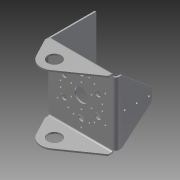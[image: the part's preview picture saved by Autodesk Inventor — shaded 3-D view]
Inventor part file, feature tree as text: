
AUTODESK INVENTOR PART (.ipt)
format: ipt  version: 2014 (Build 180170000, 170)  size: 277,504 bytes
history: native  units: in
note: dims shown in document units (in); Inventor stores cm internally (conversion verified against a paired STEP export)
features: sheet_metal_op x10, sketch x8, other x8, reference x4, fillet x2
ambient origin geometry x8: Origin, YZ Plane, XZ Plane, XY Plane, X Axis, Y Axis, Z Axis, Center Point
bodies: Solid1 (feature_tree)
feature tree (32):
  sheet_metal_op  "Face1"
  sheet_metal_op  "Flange2"
  fillet  "Fillet1"  Radius=0.125in
  sheet_metal_op  "Flange3"
  fillet  "Fillet2"  Radius=0.125in
  sheet_metal_op  "Flange4"
  sketch  "Sketch1"  dims[d1=2.3622in d2=5.25in d3=1.125in d4=0.503in d5=1.625in d6=1.31in d7=0.1875in d8=0.1875in d9=0.1875in d10=0.1875in d11=360.0deg d12=0.125in d23=0.125in]
  other  "Plate1"
  sketch  "Sketch3"  dims[d24=0.0625in]
  other  "Plate3"
  sheet_metal_op  "Bend2"
  sheet_metal_op  "Corner2"
  sketch  "Sketch5"  dims[d25=0.25in]
  reference  "Reference2"
  sketch  "Sketch6"  dims[d26=0.125in]
  sketch  "Sketch7"  dims[d27=3.0in d28=90.0deg d29=0.125in]
  other  "Plate4"
  sheet_metal_op  "Bend3"
  sheet_metal_op  "Corner3"
  sketch  "Sketch8"  dims[d30=0.5in]
  sketch  "Sketch9"  dims[d31=0.125in]
  reference  "Reference3"
  reference  "Reference4"
  reference  "Reference5"
  sketch  "Sketch11"  dims[d32=0.125in d39=1.125in d40=100.0in d41=0.0in d42=2.25in d43=0.25in d44=0.25in d45=10.0in d46=0.0in d47=0.125in d48=0.125in d49=0.0625in d50=0.25in d51=0.125in d52=3.0in d53=90.0deg d54=0.125in d55=0.5in d56=0.125in d57=0.125in d58=1.0in d59=2.125in d60=0.25in d61=0.25in d62=0.125in d63=0.0in d64=0.25in d65=0.164in d66=0.164in d67=0.164in d68=0.125in d69=0.0in d71=0.125in d72=0.0625in d73=0.25in d74=0.125in d75=4.0in d76=90.0deg d77=0.125in d78=0.5in d79=0.125in d80=0.125in]
  other  "Plate5"
  sheet_metal_op  "Bend4"
  sheet_metal_op  "Corner4"
  other  "Cut2"
  other  "Cut3"
  other  "Cut4"
  other  "Cut5"
